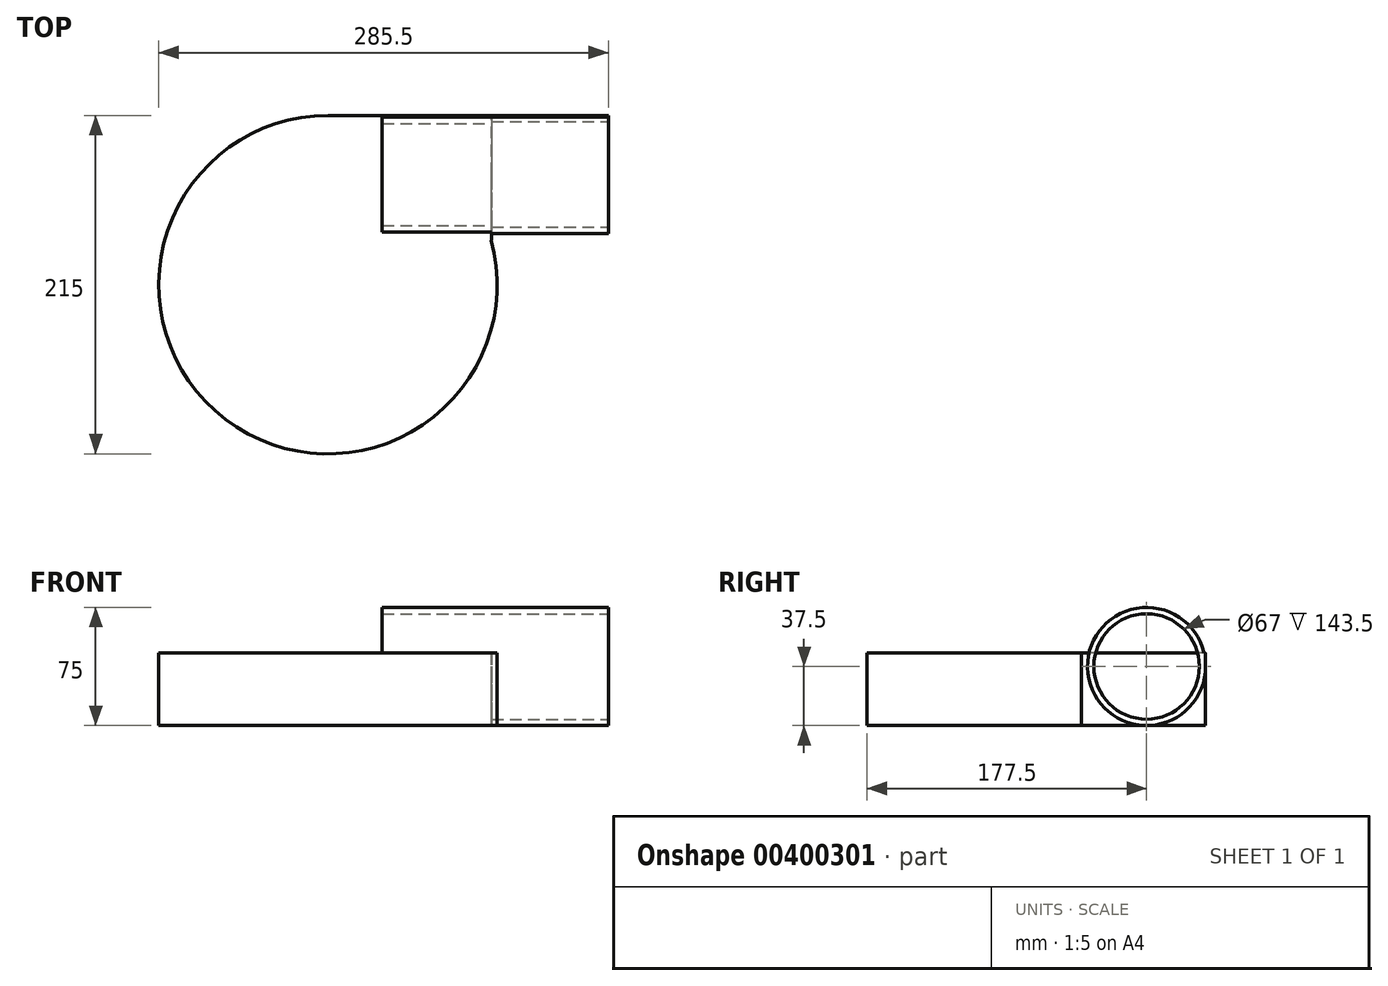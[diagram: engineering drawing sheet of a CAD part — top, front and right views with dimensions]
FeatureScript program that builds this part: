
annotation { "Feature Type Name" : "Feature", "Feature Type Description" : "" }
export const myFeature = defineFeature(function(context is Context, id is Id, definition is map)
    precondition{}
    {
        {
            var Q0;
            Q0=qCreatedBy(makeId("Top.planeOp"),FACE);
            var sketch = newSketch(context, id + "F0", { "sketchPlane" : qUnion([Q0])});
            skArc(sketch, "E0", {"start": v(0, 107.5) * mm, "mid": v(-65.16, -85.5) * mm, "end": v(103.65, 28.5) * mm});
            skLineSegment(sketch, "E1", {"start": v(0, 107.5) * mm, "end": v(178, 107.5) * mm});
            skLineSegment(sketch, "E2", {"start": v(178, 107.5) * mm, "end": v(178, 28.5) * mm});
            skLineSegment(sketch, "E3", {"start": v(178, 28.5) * mm, "end": v(103.65, 28.5) * mm});
            skSolve(sketch);
        }
        {
            var Q0;
            Q0=makeQuery(id+"F0.imprint","IMPRINT",FACE,{"disambiguationData":[TD([[makeQuery(id+"F0.imprint","IMPRINT",EDGE,{"derivedFrom":sQuery(id+"F0.wireOp",EDGE,"E0")}),1.0]])]});
            extrude(context, id + "F1", {"entities" : qUnion([Q0]), "depth" : 46 * mm});
        }
        {
            var Q0;
            Q0=makeQuery(id+"F1.opExtrude","SWEPT_FACE",FACE,{"disambiguationData":[OSD([sQuery(id+"F0.wireOp",EDGE,"E2")])]});
            var sketch = newSketch(context, id + "F2", { "sketchPlane" : qUnion([Q0])});
            skCircle(sketch, "E4", {"center": v(70, 37.5) * mm, "radius": 33.5 * mm});
            skCircle(sketch, "E5", {"center": v(70, 37.5) * mm, "radius": 37.5 * mm});
            skSolve(sketch);
        }
        {
            var Q0;
            {var subQ1=sQuery(id+"F0.wireOp",EDGE,"E2");var subQ6=makeQuery(id+"F1.opExtrude","SWEPT_EDGE",EDGE,{"disambiguationData":[OSD([subQ1,sQuery(id+"F0.wireOp",EDGE,"E3")])]});Q0=makeQuery(id+"F2.imprint","IMPRINT",FACE,{"disambiguationData":[TD([[makeQuery(id+"F2.imprint","IMPRINT",EDGE,{"derivedFrom":subQ6}),1.0]])]});}
            var Q1;
            {var subQ0=sQuery(id+"F2.wireOp",EDGE,"E5");var subQ1=sQuery(id+"F0.wireOp",EDGE,"E2");var subQ4=makeQuery(id+"F1.opExtrude","CAP_EDGE",EDGE,{"disambiguationData":[OSD([subQ1])],"isStart":true});var subQ5=makeQuery(id+"F2.imprint","INTERSECT",VERTEX,{"derivedFrom":[subQ4,subQ0]});Q1=makeQuery(id+"F2.imprint","IMPRINT",FACE,{"disambiguationData":[TD([[makeQuery(id+"F2.imprint","IMPRINT",EDGE,{"disambiguationData":[TD([[subQ5,-1.0]])],"derivedFrom":subQ0}),-1.0]])]});}
            var Q2;
            {var subQ0=sQuery(id+"F2.wireOp",EDGE,"E4");var subQ1=makeQuery(id+"F1.opExtrude","CAP_EDGE",EDGE,{"disambiguationData":[OSD([sQuery(id+"F0.wireOp",EDGE,"E2")])],"isStart":false});var subQ2=makeQuery(id+"F2.imprint","INTERSECT",VERTEX,{"disambiguationData":[OD(0.0)],"derivedFrom":[subQ1,subQ0]});Q2=makeQuery(id+"F2.imprint","IMPRINT",FACE,{"disambiguationData":[TD([[makeQuery(id+"F2.imprint","IMPRINT",EDGE,{"disambiguationData":[TD([[subQ2,1.0]])],"derivedFrom":subQ0}),1.0]])]});}
            extrude(context, id + "F3", {"entities" : qUnion([Q0, Q1, Q2]), "operationType" : NewBodyOperationType.REMOVE, "oppositeDirection" : true, "depth" : 74 * mm});
        }
        {
            var Q0;
            {var subQ0=sQuery(id+"F2.wireOp",EDGE,"E4");var subQ1=makeQuery(id+"F1.opExtrude","CAP_EDGE",EDGE,{"disambiguationData":[OSD([sQuery(id+"F0.wireOp",EDGE,"E2")])],"isStart":false});var subQ2=makeQuery(id+"F2.imprint","INTERSECT",VERTEX,{"disambiguationData":[OD(0.0)],"derivedFrom":[subQ1,subQ0]});Q0=makeQuery(id+"F2.imprint","IMPRINT",FACE,{"disambiguationData":[TD([[makeQuery(id+"F2.imprint","IMPRINT",EDGE,{"disambiguationData":[TD([[subQ2,-1.0]])],"derivedFrom":subQ0}),-1.0]])]});}
            extrude(context, id + "F4", {"entities" : qUnion([Q0]), "operationType" : NewBodyOperationType.ADD, "oppositeDirection" : true, "depth" : 143.5 * mm});
        }
    });
